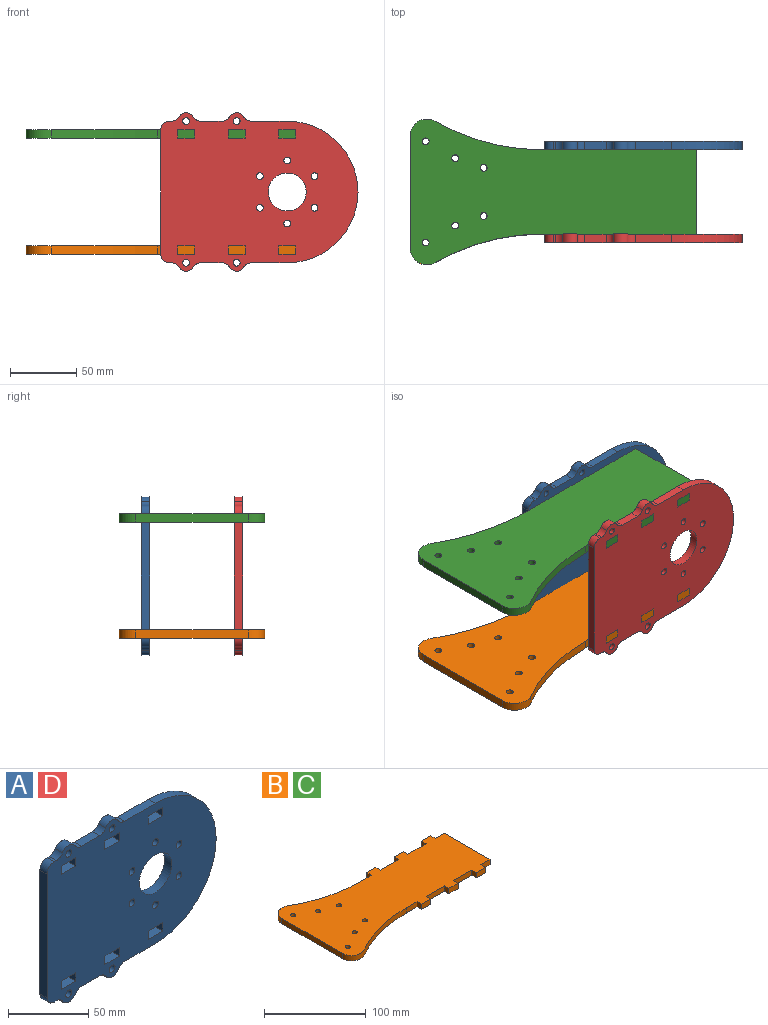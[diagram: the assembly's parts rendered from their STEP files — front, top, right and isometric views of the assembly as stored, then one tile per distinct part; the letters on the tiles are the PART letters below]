
ASSEMBLY  parts=4 mates=3
PART A: 59 faces, bbox 148.6x6.4x119.4 mm
  f0: plane 148.59x119.38mm, normal (0,-1,0), area 13562.7mm2, adj f2,f3,f4,f5,f6,f7,f8,f9
  f1: plane 148.59x119.38mm, normal (0,1,0), area 13562.7mm2, adj f2,f3,f4,f5,f6,f7,f8,f9
  f2: plane 6.35x6.35mm, normal (-1,0,0), area 40.3mm2, adj f0,f1,f3,f31
  f3: plane 12.7x6.35mm, normal (0,0,1), area 80.6mm2, adj f0,f1,f2,f4
  f4: plane 6.35x6.35mm, normal (1,0,0), area 40.3mm2, adj f0,f1,f3,f31
  f5: plane 12.7x6.35mm, normal (0,0,1), area 80.6mm2, adj f0,f1,f6,f34
  f6: plane 6.35x6.35mm, normal (1,0,0), area 40.3mm2, adj f0,f1,f5,f7
  f7: plane 12.7x6.35mm, normal (0,0,-1), area 80.6mm2, adj f0,f1,f6,f34
  f8: cylinder r=53.34mm len=106.68mm, axis (0,1,0), area 1064.1mm2, adj f0,f1,f9,f37
  f9: plane 27.1x6.35mm, normal (0,0,1), area 172.1mm2, adj f0,f1,f8,f41
  f10: cylinder r=6.35mm len=11mm, axis (0,1,0), area 84.5mm2, adj f0,f1,f41,f42
  f11: plane 16.1x6.35mm, normal (0,0,1), area 102.3mm2, adj f0,f1,f42,f43
  f12: cylinder r=6.35mm len=11mm, axis (0,1,0), area 84.5mm2, adj f0,f1,f43,f44
  f13: plane 6.35x1.7mm, normal (0,0,1), area 10.8mm2, adj f0,f1,f44,f45
  f14: plane 93.98x6.35mm, normal (-1,0,0), area 596.8mm2, adj f0,f1,f45,f46
  f15: plane 6.35x1.7mm, normal (0,0,-1), area 10.8mm2, adj f0,f1,f46,f47
  f16: cylinder r=6.35mm len=11mm, axis (0,1,0), area 84.5mm2, adj f0,f1,f47,f48
  f17: plane 16.1x6.35mm, normal (0,0,-1), area 102.3mm2, adj f0,f1,f48,f49
  f18: cylinder r=6.35mm len=11mm, axis (0,1,0), area 84.5mm2, adj f0,f1,f49,f50
  f19: plane 6.35x6.35mm, normal (-1,0,0), area 40.3mm2, adj f0,f1,f20,f38
  f20: plane 12.7x6.35mm, normal (0,0,1), area 80.6mm2, adj f0,f1,f19,f21
  f21: plane 6.35x6.35mm, normal (1,0,0), area 40.3mm2, adj f0,f1,f20,f38
  f22: plane 12.7x6.35mm, normal (0,0,1), area 80.6mm2, adj f0,f1,f23,f39
  f23: plane 6.35x6.35mm, normal (1,0,0), area 40.3mm2, adj f0,f1,f22,f24
  f24: plane 12.7x6.35mm, normal (0,0,-1), area 80.6mm2, adj f0,f1,f23,f39
  f25: cylinder r=2.55mm len=6.35mm, axis (0,1,0), area 101.8mm2, adj f0,f1
  f26: cylinder r=2.55mm len=6.35mm, axis (0,1,0), area 101.8mm2, adj f0,f1
  f27: cylinder r=2.55mm len=6.35mm, axis (0,1,0), area 101.8mm2, adj f0,f1
  f28: cylinder r=2.55mm len=6.35mm, axis (0,1,0), area 101.8mm2, adj f0,f1
  f29: cylinder r=2.55mm len=6.35mm, axis (0,1,0), area 101.8mm2, adj f0,f1
  f30: cylinder r=2.55mm len=6.35mm, axis (0,1,0), area 101.8mm2, adj f0,f1
  f31: plane 12.7x6.35mm, normal (0,0,-1), area 80.6mm2, adj f0,f1,f2,f4
  f32: cylinder r=2.55mm len=6.35mm, axis (0,1,0), area 101.8mm2, adj f0,f1
  f33: cylinder r=2.55mm len=6.35mm, axis (0,1,0), area 101.8mm2, adj f0,f1
  f34: plane 6.35x6.35mm, normal (-1,0,0), area 40.3mm2, adj f0,f1,f5,f7
  f35: cylinder r=2.55mm len=6.35mm, axis (0,1,0), area 101.8mm2, adj f0,f1
  f36: cylinder r=2.55mm len=6.35mm, axis (0,1,0), area 101.8mm2, adj f0,f1
  f37: plane 27.1x6.35mm, normal (0,0,-1), area 172.1mm2, adj f0,f1,f8,f50
  f38: plane 12.7x6.35mm, normal (0,0,-1), area 80.6mm2, adj f0,f1,f19,f21
  f39: plane 6.35x6.35mm, normal (-1,0,0), area 40.3mm2, adj f0,f1,f22,f24
  f40: cylinder r=14.29mm len=28.58mm, axis (0,1,0), area 570mm2, adj f0,f1
  f41: cylinder r=6.35mm len=6.35mm, axis (0,1,0), area 42.2mm2, adj f0,f1,f9,f10
  f42: cylinder r=6.35mm len=6.35mm, axis (0,1,0), area 42.2mm2, adj f0,f1,f10,f11
  f43: cylinder r=6.35mm len=6.35mm, axis (0,1,0), area 42.2mm2, adj f0,f1,f11,f12
  f44: cylinder r=6.35mm len=6.35mm, axis (0,1,0), area 42.2mm2, adj f0,f1,f12,f13
  f45: cylinder r=6.35mm len=6.35mm, axis (0,-1,0), area 63.3mm2, adj f0,f1,f13,f14
  f46: cylinder r=6.35mm len=6.35mm, axis (0,1,0), area 63.3mm2, adj f0,f1,f14,f15
  f47: cylinder r=6.35mm len=6.35mm, axis (0,1,0), area 42.2mm2, adj f0,f1,f15,f16
  f48: cylinder r=6.35mm len=6.35mm, axis (0,1,0), area 42.2mm2, adj f0,f1,f16,f17
  f49: cylinder r=6.35mm len=6.35mm, axis (0,1,0), area 42.2mm2, adj f0,f1,f17,f18
  f50: cylinder r=6.35mm len=6.35mm, axis (0,1,0), area 42.2mm2, adj f0,f1,f18,f37
  f51: plane 12.7x6.35mm, normal (0,0,-1), area 80.6mm2, adj f0,f1,f53,f54
  f52: plane 12.7x6.35mm, normal (0,0,1), area 80.6mm2, adj f0,f1,f53,f54
  f53: plane 6.35x6.35mm, normal (1,0,0), area 40.3mm2, adj f0,f1,f51,f52
  f54: plane 6.35x6.35mm, normal (-1,0,0), area 40.3mm2, adj f0,f1,f51,f52
  f55: plane 6.35x6.35mm, normal (1,0,0), area 40.3mm2, adj f0,f1,f56,f58
  f56: plane 12.68x6.35mm, normal (0,0,1), area 80.5mm2, adj f0,f1,f55,f57
  f57: plane 6.35x6.35mm, normal (-1,0,0), area 40.3mm2, adj f0,f1,f56,f58
  f58: plane 12.68x6.35mm, normal (0,0,-1), area 80.5mm2, adj f0,f1,f55,f57
PART B: 40 faces, bbox 215.9x109.8x6.4 mm
  f0: plane 6.35x6.35mm, normal (-1,0,0), area 40.3mm2, adj f1,f27,f31,f32
  f1: plane 12.7x6.35mm, normal (0,-1,0), area 80.6mm2, adj f0,f2,f31,f32
  f2: plane 6.35x6.35mm, normal (1,0,0), area 40.3mm2, adj f1,f3,f31,f32
  f3: plane 25.4x6.35mm, normal (0,-1,0), area 161.3mm2, adj f2,f4,f31,f32
  f4: plane 6.35x6.35mm, normal (-1,0,0), area 40.3mm2, adj f3,f5,f31,f32
  f5: plane 12.7x6.35mm, normal (0,-1,0), area 80.6mm2, adj f4,f6,f31,f32
  f6: plane 6.35x6.35mm, normal (1,0,0), area 40.3mm2, adj f5,f7,f31,f32
  f7: plane 25.4x6.35mm, normal (0,-1,0), area 161.3mm2, adj f6,f8,f31,f32
  f8: plane 6.35x6.35mm, normal (-1,0,0), area 40.3mm2, adj f7,f9,f31,f32
  f9: plane 12.7x6.35mm, normal (0,-1,0), area 80.6mm2, adj f8,f10,f31,f32
  f10: plane 6.35x6.35mm, normal (1,0,0), area 40.3mm2, adj f9,f11,f31,f32
  f11: plane 12.7x6.35mm, normal (0,-1,0), area 80.6mm2, adj f10,f12,f31,f32
  f12: plane 63.5x6.35mm, normal (1,0,0), area 403.2mm2, adj f11,f13,f31,f32
  f13: plane 12.7x6.35mm, normal (0,1,0), area 80.6mm2, adj f12,f14,f31,f32
  f14: plane 6.35x6.35mm, normal (1,0,0), area 40.3mm2, adj f13,f15,f31,f32
  f15: plane 12.7x6.35mm, normal (0,1,0), area 80.6mm2, adj f14,f16,f31,f32
  f16: plane 6.35x6.35mm, normal (-1,0,0), area 40.3mm2, adj f15,f17,f31,f32
  f17: plane 25.4x6.35mm, normal (0,1,0), area 161.3mm2, adj f16,f18,f31,f32
  f18: plane 6.35x6.35mm, normal (1,0,0), area 40.3mm2, adj f17,f19,f31,f32
  f19: plane 12.7x6.35mm, normal (0,1,0), area 80.6mm2, adj f18,f20,f31,f32
  f20: plane 6.35x6.35mm, normal (-1,0,0), area 40.3mm2, adj f19,f21,f31,f32
  f21: plane 25.4x6.35mm, normal (0,1,0), area 161.3mm2, adj f20,f22,f31,f32
  f22: plane 6.35x6.35mm, normal (1,0,0), area 40.3mm2, adj f21,f23,f31,f32
  f23: plane 12.7x6.35mm, normal (0,1,0), area 80.6mm2, adj f22,f24,f31,f32
  f24: plane 6.35x6.35mm, normal (-1,0,0), area 40.3mm2, adj f23,f28,f31,f32
  f25: cylinder r=2.55mm len=6.35mm, axis (0,0,1), area 101.8mm2, adj f31,f32
  f26: cylinder r=2.55mm len=6.35mm, axis (0,0,1), area 101.8mm2, adj f31,f32
  f27: plane 15.04x6.35mm, normal (0,-1,0), area 95.5mm2, adj f0,f30,f31,f32
  f28: plane 15.04x6.35mm, normal (0,1,0), area 95.5mm2, adj f24,f29,f31,f32
  f29: cylinder r=160.63mm len=80.22mm, axis (0,0,-1), area 533.3mm2, adj f28,f31,f32,f39
  f30: cylinder r=160.63mm len=80.22mm, axis (0,0,-1), area 533.3mm2, adj f27,f31,f32,f38
  f31: plane 215.9x109.82mm, normal (0,0,-1), area 15991.8mm2, adj f0,f1,f2,f3,f4,f5,f6,f7
  f32: plane 215.9x109.82mm, normal (0,0,1), area 15991.8mm2, adj f0,f1,f2,f3,f4,f5,f6,f7
  f33: plane 84.42x6.35mm, normal (-1,0,0), area 536.1mm2, adj f31,f32,f38,f39
  f34: cylinder r=2.55mm len=6.35mm, axis (0,0,-1), area 101.8mm2, adj f31,f32
  f35: cylinder r=2.55mm len=6.35mm, axis (0,0,-1), area 101.8mm2, adj f31,f32
  f36: cylinder r=2.55mm len=6.35mm, axis (0,0,-1), area 101.8mm2, adj f31,f32
  f37: cylinder r=2.55mm len=6.35mm, axis (0,0,-1), area 101.8mm2, adj f31,f32
  f38: cylinder r=12.7mm len=19.04mm, axis (0,0,-1), area 168.8mm2, adj f30,f31,f32,f33
  f39: cylinder r=12.7mm len=19.04mm, axis (0,0,-1), area 168.8mm2, adj f29,f31,f32,f33
PART C: same geometry as B
PART D: same geometry as A
PLACE A t=(-73.39,188.2,-14.11)mm
PLACE B t=(-73.39,118.35,-14.11)mm
PLACE C t=(-73.39,118.35,73.52)mm
PLACE D t=(-73.39,118.35,-14.11)mm
MATE fastened A.f54 <-> B.f14  axis (-1,0,0) through (383.81,153.28,-10.93)mm
MATE fastened C.f0 <-> D.f6  axis (-1,0,0) through (294.91,83.43,76.7)mm
MATE fastened A.f6 <-> C.f24  axis (1,0,0) through (294.91,153.28,76.7)mm
